# Revit family: LAMP_STORMBELL DECO + OPAL REFLECTOR
name_source: partatom
category: Luminarias
revit_build: Autodesk Revit 2015 (Build: 20140606_1530(x64)
units: mm (PartAtom-declared; Revit-internal decimal feet)

## types (16) — shared parameters
CRI = 80
Core = Core Stormbell Deco : WHITE
Diameter = 173 mm  [stored 0.567585 ft]
Fabricante = LAMP
Gear = Electronic
Height = 173 mm  [stored 0.567585 ft]
IEE = A+
Installation instructions = http://www.lamp.es
Insulation class = I
LED Lifetime = 50.000 L80 B10
Lamp = COB LED
Last update = 11/11/2020
Luminaire type = Indoor - Suspended Downlight
MacAdam = <3
Manufacturer URL = http://www.lamp.es
Manufacturer country = Spain
Manufacturer name = LAMP
Material COB = LAMP_COB
Material floron = LAMP_Aluminio cuerpo Stormbell BL
Photometric web file = Reflector glaseado core : 2338LM 3000 WHITE FLOOD
Product URL = http://www.lamp.es
Product datasheet = http://www.lamp.es
Protection rating = IP20
Type = COB CITIZEN
zero-valued in all types: Body Height

## per-type parameters (varying)
| type | Descripción | Efficacy | Finish | Initial color | Initial intensity | Modelo | Plum | Power | Power Supply | Product code | Reflector product code | Weight |
| 2338LM 3000 WHITE FLOOD | STORMBELL DECO 3000 WW FL WH. | 89 lm/W | Shiny white | 3000 K | 2338 lm | ST117030FL830NOW | 26 W | 25 W | 220-240V 50-60Hz | ST117030FL830NOW | 10400120 | 4.50 kg |
| 2338LM 3000 BLACK FLOOD | STORMBELL DECO 3000 WW FL BK. | 89 lm/W | Shiny black | 3000 K | 2338 lm | ST117030FL830NOB | 26 W | 25 W | 220-240V 50-60Hz | ST117030FL830NOB | 10400120 | 4.50 kg |
| 2402LM 4000 WHITE FLOOD | STORMBELL DECO 3000 NW FL WH. | 91 lm/W | Shiny white | 4000 K | 2402 lm | ST117030FL840NOW | 26 W | 25 W | 220-240V 50-60Hz | ST117030FL840NOW | 10400120 | 4.50 kg |
| 2402LM 4000 BLACK FLOOD | STORMBELL DECO 3000 NW FL BK. | 91 lm/W | Shiny black | 4000 K | 2402 lm | ST117030FL840NOB | 26 W | 25 W | 220-240V 50-60Hz | ST117030FL840NOB | 10400120 | 4.50 kg |
| 2567LM 3000 WHITE WIDE FLOOD | STORMBELL DECO 3000 WW WFL WH. | 98 lm/W | Shiny white | 3000 K | 2567 lm | ST117030WF830NOW | 26 W | 25 W | 220-240V 50-60Hz | ST117030WF830NOW | 10400120 | 4.50 kg |
| 2567LM 3000 BLACK WIDE FLOOD | STORMBELL DECO 3000 WW WFL BK. | 98 lm/W | Shiny black | 3000 K | 2567 lm | ST117030WF830NOB | 26 W | 25 W | 220-240V 50-60Hz | ST117030WF830NOB | 10400120 | 4.50 kg |
| 2638LM 4000 WHITE WIDE FLOOD | STORMBELL DECO 3000 NW WFL WH. | 100 lm/W | Shiny white | 4000 K | 2638 lm | ST117030WF840NOW | 26 W | 25 W | 220-240V 50-60Hz | ST117030WF840NOW | STBE420OP | 4.50 kg |
| 2638LM 4000 BLACK WIDE FLOOD | STORMBELL DECO 3000 NW WFL BK. | 100 lm/W | Shiny black | 4000 K | 2638 lm | ST117030WF840NOB | 26 W | 25 W | 220-240V 50-60Hz | ST117030WF840NOB | STBE420OP | 4.50 kg |
| 3691LM 3000 WHITE FLOOD | STORMBELL DECO 5000 WW FL WH. | 78 lm/W | Shiny white | 3000 K | 3691 lm | ST117050FL830NOW | 47 W | 44 W | 100-240V 50-60Hz | ST117050FL830NOW | STBE420OP | 4.59 kg |
| 3691LM 3000 BLACK FLOOD | STORMBELL DECO 5000 WW FL BK. | 78 lm/W | Shiny black | 3000 K | 3691 lm | ST117050FL830NOB | 47 W | 44 W | 100-240V 50-60Hz | ST117050FL830NOB | STBE420OP | 4.59 kg |
| 3793LM 4000 WHITE FLOOD | STORMBELL DECO 5000 NW FL WH. | 80 lm/W | Shiny white | 4000 K | 3793 lm | ST117050FL840NOW | 47 W | 44 W | 100-240V 50-60Hz | ST117050FL840NOW | STBE420OP | 4.59 kg |
| 3793LM 4000 BLACK FLOOD | STORMBELL DECO 5000 NW FL BK. | 80 lm/W | Shiny black | 4000 K | 3793 lm | ST117050FL840NOB | 47 W | 44 W | 100-240V 50-60Hz | ST117050FL840NOB | STBE420OP | 4.59 kg |
| 4042LM 3000 WHITE WIDE FLOOD | STORMBELL DECO 5000 WW WFL WH. | 85 lm/W | Shiny white | 3000 K | 4042 lm | ST117050WF830NOW | 47 W | 44 W | 100-240V 50-60Hz | ST117050WF830NOW | STBE420OP | 4.59 kg |
| 4042LM 3000 BLACK WIDE FLOOD | STORMBELL DECO 5000 WW WFL BK. | 85 lm/W | Shiny black | 3000 K | 4042 lm | ST117050WF830NOB | 47 W | 44 W | 100-240V 50-60Hz | ST117050WF830NOB | STBE420OP | 4.59 kg |
| 4154LM 4000 WHITE WIDE FLOOD | STORMBELL DECO 5000 NW WFL WH. | 88 lm/W | Shiny white | 4000 K | 4154 lm | ST117050WF840NOW | 47 W | 44 W | 100-240V 50-60Hz | ST117050WF840NOW | STBE420OP | 4.59 kg |
| 4154LM 4000 BLACK WIDE FLOOD | STORMBELL DECO 5000 NW WFL BK. | 88 lm/W | Shiny black | 4000 K | 4154 lm | ST117050WF840NOB | 47 W | 44 W | 100-240V 50-60Hz | ST117050WF840NOB | STBE420OP | 4.59 kg |

note: [stored X ft] marks values corroborated as IEEE doubles in the binary element streams (Revit-internal decimal feet)
